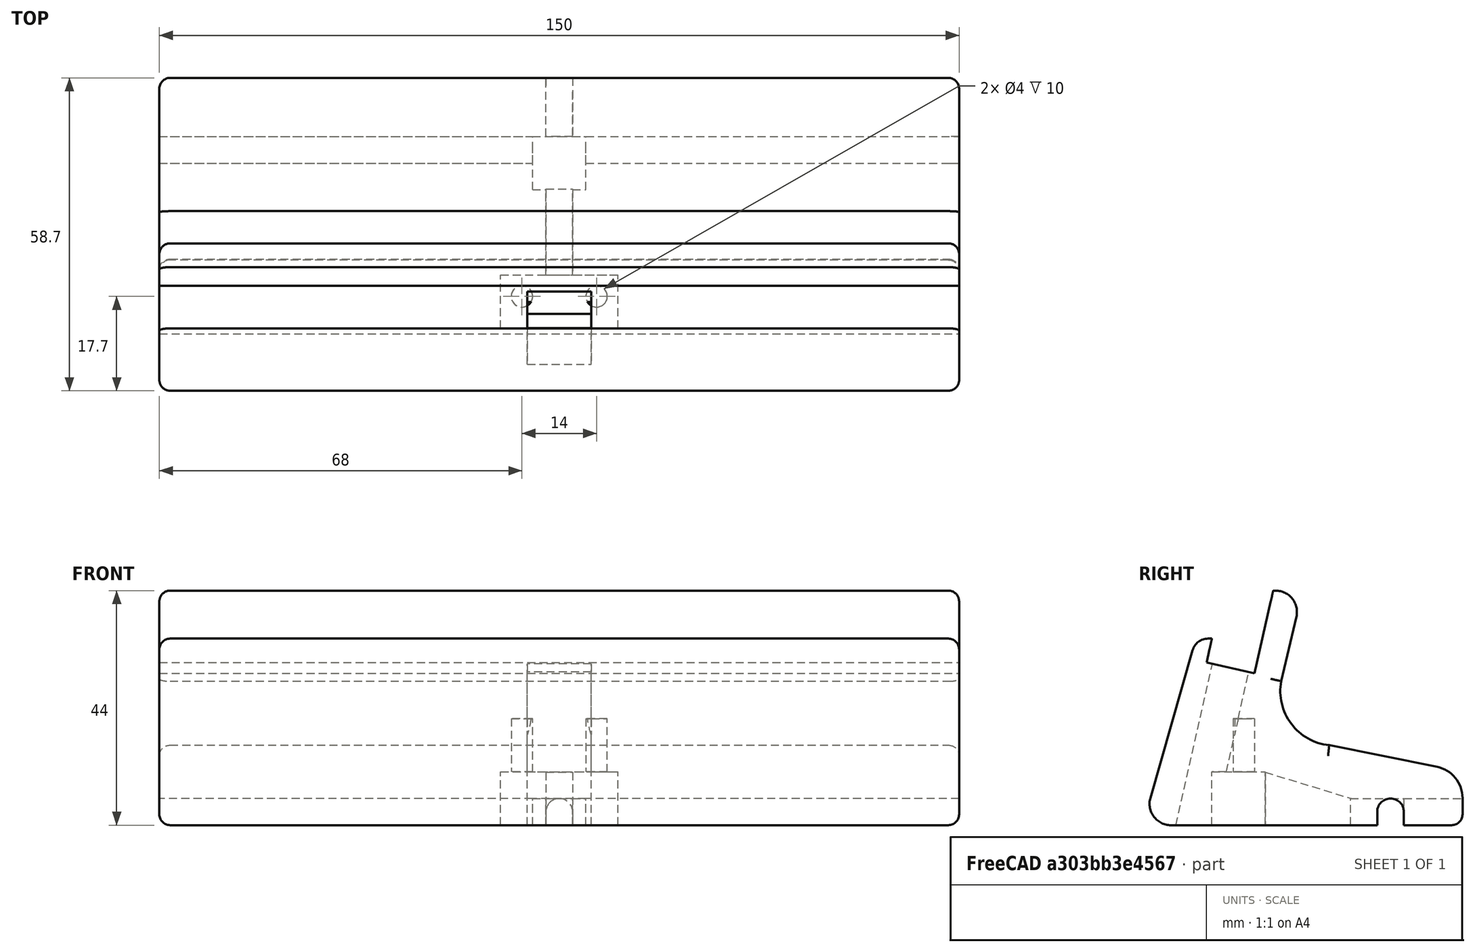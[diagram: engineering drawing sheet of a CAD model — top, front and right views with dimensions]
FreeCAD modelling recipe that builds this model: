
FCSTD DOCUMENT  (FreeCAD 0.21RUnknown)
Label: tablet.stand
License: All rights reserved
LicenseURL: https://en.wikipedia.org/wiki/All_rights_reserved
objects: PartDesign::Fillet×7, PartDesign::SubtractiveBox×6, PartDesign::SubtractiveCylinder×4, App::MeasureDistance×2, Mesh::Feature×1, Sketcher::SketchObject×1, PartDesign::Pad×1, PartDesign::Body×1
note: 38 computed .brp shape members not serialized (recipe doc carries the construction recipe); baked Part::Feature solids carry a one-line shape summary decoded from their .brp

FEATURE [Mesh::Feature] NEXUS_10_DOCK
  Placement = pos=(0,0,0) rot=(1,0,0;1.5708rad)
FEATURE [App::MeasureDistance] Distance  label="Width"
  Distance = 50
  P1 = (150,-50,0)
  P2 = (150,0,0)
FEATURE [Sketcher::SketchObject] Sketch
  FullyConstrained = true
  MapMode = 5
  Placement = pos=(0,0,0) rot=(0.57735,0.57735,0.57735;2.0944rad)
  Support = -> [YZ_Plane]
  sketch-geometry (11):
    g0: LineSegment StartX=0 StartY=0 StartZ=0 EndX=-60 EndY=0 EndZ=0
    g1: LineSegment StartX=-60 StartY=0 StartZ=0 EndX=-50 EndY=35 EndZ=0
    g2: LineSegment StartX=-50 StartY=35 StartZ=0 EndX=-47 EndY=35 EndZ=0
    g3: LineSegment StartX=-47 StartY=35 StartZ=0 EndX=-48 EndY=30.5 EndZ=0
    g4: LineSegment StartX=-48 StartY=30.5 StartZ=0 EndX=-39 EndY=28.5 EndZ=0
    g5: LineSegment StartX=-34 StartY=27 StartZ=0 EndX=-30 EndY=44 EndZ=0
    g6: LineSegment StartX=-35.5 StartY=44 StartZ=0 EndX=-30 EndY=44 EndZ=0
    g7: LineSegment StartX=-25 StartY=15 StartZ=0 EndX=0 EndY=10 EndZ=0
    g8: LineSegment StartX=0 StartY=10 StartZ=0 EndX=0 EndY=0 EndZ=0
    g9: LineSegment StartX=-35.5 StartY=44 StartZ=0 EndX=-39 EndY=28.5 EndZ=0
    g10: ArcOfCircle CenterX=-23.9612 CenterY=25.1541 CenterZ=0 NormalX=0 NormalY=0 NormalZ=1 AngleXU=0 Radius=10.2071 StartAngle=2.95975 EndAngle=4.61044
  constraints (33):
    c: Horizontal(g0)
    c: Coincident(g8,g7)
    c: DistanceY(g8,g8) = 10
    c: Coincident(g-1,g8)
    c: Coincident(g8,g0)
    c: DistanceX(g0,g0) = 60
    c: Coincident(g0,g1)
    c: DistanceY(g-1,g7) = 15
    c: DistanceX(g1,g-1) = 50
    c: DistanceY(g-1,g1) = 35
    c: DistanceX(g8,g8) = 0
    c: DistanceX(g7,g-1) = 25
    c: Coincident(g7,g10)
    c: DistanceX(g10,g-1) = 34
    c: DistanceY(g-1,g10) = 27
    c: Distance(g10,g0) = 34.74
    c: Coincident(g10,g5)
    c: DistanceX(g5,g-1) = 30
    c: DistanceY(g-1,g5) = 44
    c: Coincident(g5,g6)
    c: DistanceX(g6,g-1) = 35.5
    c: Coincident(g6,g9)
    c: DistanceX(g9,g-1) = 39
    c: DistanceY(g-1,g9) = 28.5
    c: Coincident(g9,g4)
    c: DistanceX(g4,g4) = 9
    c: DistanceY(g-1,g4) = 30.5
    c: Coincident(g1,g2)
    c: Coincident(g4,g3)
    c: Parallel(g-1,g2)
    c: DistanceX(g1,g2) = 3
    c: Coincident(g2,g3)
    c: Parallel(g-1,g6)
FEATURE [App::MeasureDistance] Distance001  label="Base"
  Distance = 29.5958
  P1 = (0,-43.4479,29.4884)
  P2 = (0,-45.9669,0)
FEATURE [PartDesign::Pad] Pad
  Direction = (1,-2e-16,3e-16)
  Length = 150
  Length2 = 10
  Placement = pos=(0,0,0) rot=(1,1,1;2.0944rad)
  Profile = -> Sketch
  ReferenceAxis = -> Sketch [N_Axis]
  Type = 0
FEATURE [PartDesign::SubtractiveBox] Box
  AttacherType = Attacher::AttachEngine3D
  AttachmentOffset = pos=(69,-54.3,-2.5) rot=(-1,0,0;0.221657rad)
  BaseFeature = -> Pad
  Height = 35
  Length = 12
  MapMode = 5
  Placement = pos=(69,-54.3,-2.5) rot=(-1,0,0;0.221657rad)
  Support = -> [XY_Plane]
  Width = 7
FEATURE [PartDesign::SubtractiveBox] Box001
  AttacherType = Attacher::AttachEngine3D
  AttachmentOffset = pos=(64,-47,0) rot=(0,0,1;0rad)
  BaseFeature = -> Box
  Height = 10
  Length = 22
  MapMode = 5
  Placement = pos=(64,-47,0) rot=(0,0,1;0rad)
  Support = -> [XY_Plane]
  Width = 10
FEATURE [PartDesign::SubtractiveCylinder] Cylinder
  Angle = 360
  AttacherType = Attacher::AttachEngine3D
  AttachmentOffset = pos=(68,-41,10) rot=(0,0,1;0rad)
  BaseFeature = -> Box001
  FirstAngle = 0
  Height = 10
  MapMode = 5
  Placement = pos=(68,-41,10) rot=(0,0,1;0rad)
  Radius = 2
  SecondAngle = 0
  Support = -> [XY_Plane]
FEATURE [PartDesign::SubtractiveCylinder] Cylinder001
  Angle = 360
  AttacherType = Attacher::AttachEngine3D
  AttachmentOffset = pos=(82,-41,10) rot=(0,0,1;0rad)
  BaseFeature = -> Cylinder
  FirstAngle = 0
  Height = 10
  MapMode = 5
  Placement = pos=(82,-41,10) rot=(0,0,1;0rad)
  Radius = 2
  SecondAngle = 0
  Support = -> [XY_Plane]
FEATURE [PartDesign::SubtractiveBox] Box002
  AttacherType = Attacher::AttachEngine3D
  AttachmentOffset = pos=(72.5,-40,0.4) rot=(-1,0,0;0.296706rad)
  BaseFeature = -> Cylinder001
  Height = 10
  Length = 5
  MapMode = 5
  Placement = pos=(72.5,-40,0.4) rot=(-1,0,0;0.296706rad)
  Support = -> [XY_Plane]
  Width = 22
FEATURE [PartDesign::SubtractiveBox] Box003
  AttacherType = Attacher::AttachEngine3D
  AttachmentOffset = pos=(70,-21,0) rot=(0,0,1;0rad)
  BaseFeature = -> Box002
  Height = 5
  Length = 10
  MapMode = 5
  Placement = pos=(70,-21,0) rot=(0,0,1;0rad)
  Support = -> [XY_Plane]
  Width = 10
FEATURE [PartDesign::SubtractiveCylinder] Cylinder002
  Angle = 360
  AttacherType = Attacher::AttachEngine3D
  AttachmentOffset = pos=(75,2.5,0) rot=(0,0,1;0rad)
  BaseFeature = -> Box003
  FirstAngle = 0
  Height = 11
  MapMode = 5
  Placement = pos=(75,6e-16,2.5) rot=(1,0,0;1.5708rad)
  Radius = 2.5
  SecondAngle = 0
  Support = -> [XZ_Plane]
FEATURE [PartDesign::SubtractiveCylinder] Cylinder003
  Angle = 360
  AttacherType = Attacher::AttachEngine3D
  AttachmentOffset = pos=(-13.5,2.5,0) rot=(0,0,1;0rad)
  BaseFeature = -> Cylinder002
  FirstAngle = 0
  Height = 150
  MapMode = 5
  Placement = pos=(-3.6e-15,-13.5,2.5) rot=(0.57735,0.57735,0.57735;2.0944rad)
  Radius = 2.5
  SecondAngle = 0
  Support = -> [YZ_Plane]
FEATURE [PartDesign::SubtractiveBox] Box004
  AttacherType = Attacher::AttachEngine3D
  AttachmentOffset = pos=(-16,0,0) rot=(0,0,1;0rad)
  BaseFeature = -> Cylinder003
  Height = 150
  Length = 5
  MapMode = 5
  Placement = pos=(-3.6e-15,-16,3.6e-15) rot=(0.57735,0.57735,0.57735;2.0944rad)
  Support = -> [YZ_Plane]
  Width = 2.5
FEATURE [PartDesign::SubtractiveBox] Box005
  AttacherType = Attacher::AttachEngine3D
  AttachmentOffset = pos=(72.5,-11,0) rot=(0,0,1;0rad)
  BaseFeature = -> Box004
  Height = 2.5
  Length = 5
  MapMode = 5
  Placement = pos=(72.5,-11,0) rot=(0,0,1;0rad)
  Support = -> [XY_Plane]
  Width = 11
FEATURE [PartDesign::Fillet] Fillet
  Base = -> Box005 [Edge5]
  BaseFeature = -> Box005
  Placement = pos=(72.5,-11,0) rot=(0,0,1;0rad)
  Radius = 4
  SupportTransform = false
  UseAllEdges = false
FEATURE [PartDesign::Fillet] Fillet001
  Base = -> Fillet [Edge46]
  BaseFeature = -> Fillet
  Placement = pos=(72.5,-11,0) rot=(0,0,1;0rad)
  Radius = 3
  SupportTransform = false
  UseAllEdges = false
FEATURE [PartDesign::Fillet] Fillet002
  Base = -> Fillet001 [Edge76]
  BaseFeature = -> Fillet001
  Placement = pos=(72.5,-11,0) rot=(0,0,1;0rad)
  Radius = 6
  SupportTransform = false
  UseAllEdges = false
FEATURE [PartDesign::Fillet] Fillet003
  Base = -> Fillet002 [Edge46]
  BaseFeature = -> Fillet002
  Placement = pos=(72.5,-11,0) rot=(0,0,1;0rad)
  Radius = 4
  SupportTransform = false
  UseAllEdges = false
FEATURE [PartDesign::Fillet] Fillet004
  Base = -> Fillet003 [Edge44,Edge4]
  BaseFeature = -> Fillet003
  Placement = pos=(72.5,-11,0) rot=(0,0,1;0rad)
  Radius = 2
  SupportTransform = false
  UseAllEdges = false
FEATURE [PartDesign::Fillet] Fillet005
  Base = -> Fillet004 [Edge55,Edge13]
  BaseFeature = -> Fillet004
  Placement = pos=(72.5,-11,0) rot=(0,0,1;0rad)
  Radius = 2
  SupportTransform = false
  UseAllEdges = false
FEATURE [PartDesign::Fillet] Fillet006
  Base = -> Fillet005 [Edge1,Edge120]
  BaseFeature = -> Fillet005
  Placement = pos=(72.5,-11,0) rot=(0,0,1;0rad)
  Radius = 2
  SupportTransform = false
  UseAllEdges = false
FEATURE [PartDesign::Body] Body
  Group = -> [Sketch,Pad,Box,Box001,Cylinder,Cylinder001,Box002,Box003,Cylinder002,Cylinder003,Box004,Box005,Fillet,Fillet001,Fillet002,Fillet003,Fillet004,Fillet005,Fillet006]
  Origin = -> Origin
  Tip = -> Fillet006
